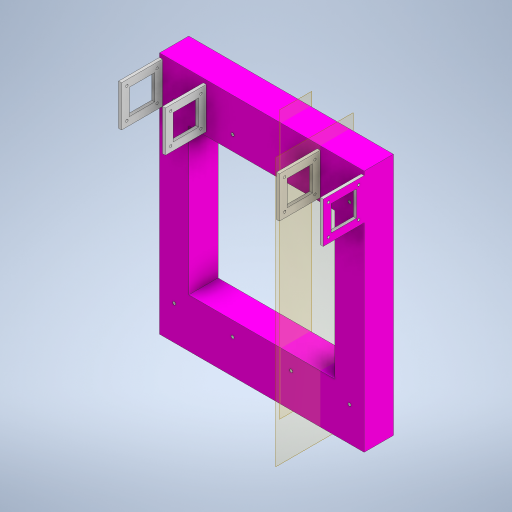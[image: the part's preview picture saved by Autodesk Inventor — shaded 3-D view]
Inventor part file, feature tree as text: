
AUTODESK INVENTOR PART (.ipt)
format: ipt  version: 2024.2 (Build 282272000, 272)  size: 405,504 bytes
history: native  units: mm
features: extrude x4, sketch x4, other x3, mirror x2
ambient origin geometry x8: Origin, YZ Plane, XZ Plane, XY Plane, X Axis, Y Axis, Z Axis, Center Point
bodies: Body1 (feature_tree)
feature tree (13):
  other  "Твердое тело1"
  extrude  "Выдавливание1"  Depth=210.0mm
  extrude  "Выдавливание2"  Depth=250.0mm
  other  "РабПлоскость4"
  extrude  "Выдавливание5"  Depth=150.0mm
  mirror  "Зеркальное отражение3"
  other  "РабПлоскость5"
  extrude  "Выдавливание6"  Depth=150.0mm
  mirror  "Зеркальное отражение4"
  sketch  "Эскиз1"
  sketch  "Эскиз2"
  sketch  "Эскиз7"
  sketch  "Эскиз8"
